# Revit family: J2 PET Felt Switch Baffle System A
name_source: partatom
category: Specialty Equipment
units: mm (PartAtom-declared; Revit-internal decimal feet)

## family parameters
Always vertical = Yes
Cut with Voids When Loaded = No
Part Type = Normal
Room Calculation Point = No
Round Connector Dimension = Use Diameter
Shared = No
Work Plane-Based = No

## types (2) — shared parameters
Baffle Height (Max. 3'-11") = 0' - 11"
Baffle Height @ Narrow End = 0' - 6"
Baffles = 8
Default Elevation = 0' - 0"
End Spacing = 0' - 6"
Felt Color = <By Category>
Manufacturer = J2 Systems
Model = Switch Baffle System A
Nominal Length (Max. 8'-0") = 8' - 0"
Product Line = Ceiling System
Release Date = 2019
Style Number = CSBSSW-A
URL = https://www.j2systems.net

## per-type parameters (varying)
| type | Number of Support Rails Needed | Overall Width (Max. 7'-11") |
| Switch Baffle System A 8'-0"x7'-11"x11" | 3 | 7' - 11" |
| Switch Baffle System A 8'-0"x3'-11"x11" | 2 | 3' - 11" |

## geometry (parser evidence)
native form markers: Sweep x9
no freeform markers — native parametric forms only
